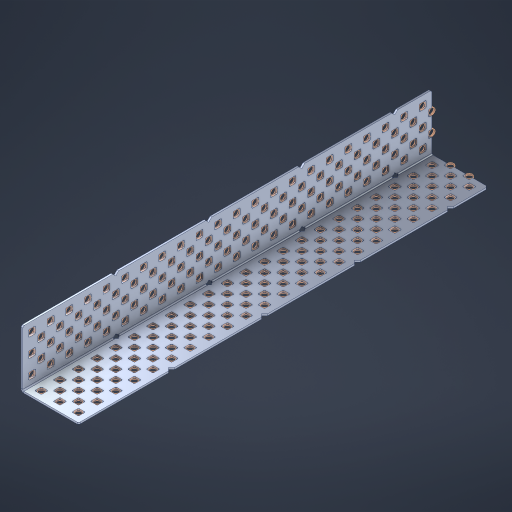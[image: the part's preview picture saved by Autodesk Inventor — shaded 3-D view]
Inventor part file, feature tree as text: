
AUTODESK INVENTOR PART (.ipt)
format: ipt  version: 2023 (Build 270158000, 158)  size: 2,348,544 bytes
history: native  units: in
note: dims shown in document units (in); Inventor stores cm internally (conversion verified against a paired STEP export)
features: other x226, extrude x218, sheet_metal_op x8, sketch x7, pattern_linear x3, mirror x1, chamfer x1
ambient origin geometry x8: Origin, YZ Plane, XZ Plane, XY Plane, X Axis, Y Axis, Z Axis, Center Point
bodies: Solid1 (feature_tree), Body (feature_tree)
feature tree (464):
  sheet_metal_op  "Flanges"
  sheet_metal_op  "Body Pattern"
  pattern_linear  "Center Double"  Spacing1=1.5in  [1 undecoded]
  pattern_linear  "Center Pattern"  Spacing1=0.1875in  [1 undecoded]
  other  "Arc Length"
  pattern_linear  "Notch Pattern"  Spacing1=0.0469in  [1 undecoded]
  other  "Diagonal Plane"
  mirror  "Everything Mirrored"
  chamfer  "End Chamfer"
  sketch  "Sketch1"  dims[d0=1.5in]
  other  "Plate1"
  sketch  "Sketch2"  dims[d1=11.0in]
  other  "Plate2"
  sheet_metal_op  "Bend1"
  sheet_metal_op  "Corner1"
  sketch  "Sketch8"  dims[d2=0.0469in]
  sketch  "Sketch9"  dims[d3=0.0469in]
  other  "Srf91"
  sheet_metal_op  "Body Pattern Sketch"
  other  "Srf92"
  sketch  "Sketch13"  dims[d4=0.0234in]
  sketch  "Sketch15"  dims[d5=0.0938in]
  sketch  "Sketch16"  dims[d6=0.0469in d7=1.5in d8=90.0deg d9=0.0312in d10=0.1875in d11=0.0469in d12=0.0469in d49=0.182in d50=0.02in d52=0.25in d53=0.0469in d54=0.0in d55=0.172in d56=1.0in d57=0.0in d85=0.1473in d86=0.1659in d89=0.0469in d90=0.0in d91=0.04in d92=0.0491in d95=2.5in d96=0.04in d97=0.25in d98=45.0deg d106=0.182in d107=0.02in d110=0.0469in d111=0.0in d112=0.172in d113=0.5in d114=0.0in d117=0.5in d126=0.0491in d127=0.1227in d128=0.08in d129=0.04in d130=2.5in d131=0.25in d132=8.6614in d134=0.5in d135=1.1811in d137=0.5in d140=0.5in d141=1.0in d142=0.3937in d144=0.5in d145=0.071in d146=0.7874in d148=0.5in]
  other  "Srf786"
  other  "Srf856"
  other  "Srf889"
  other  "Srf890"
  other  "Srf891"
  other  "Srf1275"
  other  "Srf1276"
  other  "Srf1278"
  other  "Srf1277"
  other  "Srf1285"
  other  "Srf1286"
  other  "Srf1287"
  other  "Srf1445"
  other  "Srf1446"
  other  "Srf1447"
  other  "Srf1448"
  other  "Srf1449"
  other  "Srf1537"
  other  "Srf1538"
  other  "Srf1539"
  other  "Srf1540"
  other  "Srf1541"
  other  "Srf1807"
  other  "Srf1808"
  other  "Srf1809"
  other  "Srf1810"
  other  "Srf1811"
  other  "Srf1812"
  other  "Srf1813"
  other  "Srf1814"
  other  "Srf1815"
  other  "Srf1816"
  other  "Srf1817"
  other  "Srf1818"
  other  "Srf1819"
  other  "Srf1959"
  other  "Srf1960"
  other  "Srf1961"
  other  "Srf1962"
  other  "Srf1963"
  other  "Srf1964"
  other  "Srf1965"
  other  "Srf1966"
  other  "Srf1967"
  other  "Srf1968"
  other  "Srf1969"
  other  "Srf1970"
  other  "Srf1971"
  other  "Srf2009"
  other  "Srf2010"
  other  "Srf2011"
  other  "Srf2012"
  other  "Srf2013"
  other  "Srf2014"
  other  "Srf2015"
  other  "Srf2016"
  other  "Srf2017"
  other  "Srf2018"
  other  "Srf2019"
  other  "Srf2020"
  other  "Srf2021"
  other  "Srf2022"
  other  "Srf2023"
  other  "Srf2024"
  other  "Srf2025"
  other  "Srf2026"
  other  "Srf2027"
  other  "Srf2028"
  other  "Srf2029"
  other  "Srf2030"
  other  "Srf2043"
  other  "Srf2044"
  other  "Srf2045"
  other  "Srf2046"
  other  "Srf2047"
  other  "Srf2048"
  other  "Srf2049"
  other  "Srf2050"
  other  "Srf2051"
  other  "Srf2052"
  other  "Srf2053"
  other  "Srf2054"
  other  "Srf2055"
  other  "Srf2056"
  other  "Srf2057"
  other  "Srf2058"
  other  "Srf2059"
  other  "Srf2060"
  other  "Srf2061"
  other  "Srf2062"
  other  "Srf2063"
  other  "Srf2076"
  other  "Srf2077"
  other  "Srf2078"
  other  "Srf2079"
  other  "Srf2080"
  other  "Srf2081"
  other  "Srf2082"
  other  "Srf2083"
  other  "Srf2084"
  other  "Srf2085"
  other  "Srf2086"
  other  "Srf2087"
  other  "Srf2088"
  other  "Srf2089"
  other  "Srf2090"
  other  "Srf2091"
  other  "Srf2092"
  other  "Srf2093"
  other  "Srf2094"
  other  "Srf2095"
  other  "Srf2096"
  other  "Srf2097"
  other  "Srf2098"
  other  "Srf2099"
  other  "Srf2100"
  other  "Srf2101"
  other  "Srf2102"
  other  "Srf2103"
  other  "Srf2104"
  other  "Srf2105"
  other  "Srf2106"
  other  "Srf2107"
  other  "Srf2108"
  other  "Srf2109"
  other  "Srf2110"
  other  "Srf2111"
  other  "Srf2112"
  other  "Srf2113"
  other  "Srf2114"
  other  "Srf2115"
  other  "Srf2116"
  other  "Srf2117"
  other  "Srf2118"
  other  "Srf2119"
  other  "Srf2120"
  other  "Srf2121"
  other  "Srf2122"
  other  "Srf2123"
  other  "Srf2124"
  other  "Srf2125"
  other  "Srf2126"
  other  "Srf2127"
  other  "Srf2128"
  other  "Srf2129"
  other  "Srf2130"
  other  "Srf2131"
  other  "Srf2132"
  other  "Srf2133"
  other  "Srf2134"
  other  "Srf2135"
  other  "Srf2136"
  other  "Srf2137"
  other  "Srf2138"
  other  "Srf2139"
  other  "Srf2179"
  other  "Srf2180"
  other  "Srf2181"
  other  "Srf2182"
  other  "Srf2183"
  other  "Srf2184"
  other  "Srf2185"
  other  "Srf2186"
  other  "Srf2187"
  other  "Srf2188"
  other  "Srf2189"
  other  "Srf2190"
  other  "Srf2191"
  other  "Srf2192"
  other  "Srf2193"
  other  "Srf2194"
  other  "Srf2195"
  other  "Srf2196"
  other  "Srf2197"
  other  "Srf2198"
  other  "Srf2199"
  other  "Srf2200"
  other  "Srf2201"
  other  "Srf2202"
  other  "Srf2203"
  other  "Srf2204"
  other  "Srf2205"
  other  "Srf2206"
  other  "Srf2207"
  other  "Srf2208"
  other  "Srf2209"
  other  "Srf2210"
  other  "Srf2211"
  other  "Srf2212"
  other  "Srf2213"
  other  "Srf2214"
  other  "Srf2215"
  other  "Srf2216"
  other  "Srf2217"
  other  "Srf2218"
  other  "Srf2219"
  other  "Srf2220"
  other  "Srf2221"
  other  "Srf2222"
  other  "Srf2223"
  other  "Srf2224"
  other  "Srf2225"
  other  "Srf2226"
  other  "Srf2227"
  other  "Srf2228"
  other  "Srf2229"
  other  "Srf2230"
  other  "Srf2231"
  other  "Srf2232"
  other  "Srf2233"
  other  "Srf2234"
  other  "Srf2235"
  other  "Srf2236"
  other  "Srf2237"
  other  "Srf2238"
  other  "Srf2239"
  other  "Srf2240"
  other  "Srf2241"
  sheet_metal_op  "Body Stamp"
  sheet_metal_op  "Body Circle"
  other  "Center Stamp"
  other  "Center Circle"
  sheet_metal_op  "Notch"
  extrude  "ExtrusionSrf92"  Depth=0.0469in
  extrude  "ExtrusionSrf856"  Depth=0.182in
  extrude  "ExtrusionSrf889"  Depth=0.02in
  extrude  "ExtrusionSrf890"  Depth=0.25in
  extrude  "ExtrusionSrf891"  Depth=0.0469in
  extrude  "ExtrusionSrf1275"  TaperAngle=0.0deg  [1 undecoded]
  extrude  "ExtrusionSrf1276"  Depth=0.5in
  extrude  "ExtrusionSrf1277"  Depth=1.0in TaperAngle=0.0deg
  extrude  "ExtrusionSrf1345"  Depth=0.5in
  extrude  "ExtrusionSrf1346"  Depth=0.5in
  extrude  "ExtrusionSrf1347"  Depth=0.0469in
  extrude  "ExtrusionSrf1348"  Depth=0.5in TaperAngle=0.0deg
  extrude  "ExtrusionSrf1445"  Depth=0.5in
  extrude  "ExtrusionSrf1446"  Depth=0.25in TaperAngle=45.0deg
  extrude  "ExtrusionSrf1447"  Depth=0.182in
  extrude  "ExtrusionSrf1448"  Depth=0.02in
  extrude  "ExtrusionSrf1449"  Depth=0.0469in
  extrude  "ExtrusionSrf1537"  TaperAngle=0.0deg  [1 undecoded]
  extrude  "ExtrusionSrf1538"  Depth=0.5in
  extrude  "ExtrusionSrf1539"  Depth=0.5in TaperAngle=0.0deg
  extrude  "ExtrusionSrf1540"  Depth=0.5in
  extrude  "ExtrusionSrf1541"  Depth=0.5in
  extrude  "ExtrusionSrf1807"  Depth=0.5in
  extrude  "ExtrusionSrf1808"  Depth=0.5in
  extrude  "ExtrusionSrf1809"  Depth=0.5in
  extrude  "ExtrusionSrf1810"  Depth=0.5in
  extrude  "ExtrusionSrf1811"  Depth=0.25in
  extrude  "ExtrusionSrf1812"  Depth=0.5in
  extrude  "ExtrusionSrf1813"  Depth=0.5in
  extrude  "ExtrusionSrf1814"  Depth=0.5in
  extrude  "ExtrusionSrf1815"  Depth=1.0in
  extrude  "ExtrusionSrf1816"  Depth=0.3937in
  extrude  "ExtrusionSrf1817"  Depth=0.5in
  extrude  "ExtrusionSrf1818"  Depth=0.5in
  extrude  "ExtrusionSrf1819"  [1 undecoded]
  extrude  "ExtrusionSrf1959"  [1 undecoded]
  extrude  "ExtrusionSrf1960"  [1 undecoded]
  extrude  "ExtrusionSrf1961"  [1 undecoded]
  extrude  "ExtrusionSrf1962"  [1 undecoded]
  extrude  "ExtrusionSrf1963"  [1 undecoded]
  extrude  "ExtrusionSrf1964"  [1 undecoded]
  extrude  "ExtrusionSrf1965"  [1 undecoded]
  extrude  "ExtrusionSrf1966"  [1 undecoded]
  extrude  "ExtrusionSrf1967"  [1 undecoded]
  extrude  "ExtrusionSrf1968"  [1 undecoded]
  extrude  "ExtrusionSrf1969"  [1 undecoded]
  extrude  "ExtrusionSrf1970"  [1 undecoded]
  extrude  "ExtrusionSrf1971"  [1 undecoded]
  extrude  "ExtrusionSrf2009"  [1 undecoded]
  extrude  "ExtrusionSrf2010"  [1 undecoded]
  extrude  "ExtrusionSrf2011"  [1 undecoded]
  extrude  "ExtrusionSrf2012"  [1 undecoded]
  extrude  "ExtrusionSrf2013"  [1 undecoded]
  extrude  "ExtrusionSrf2014"  [1 undecoded]
  extrude  "ExtrusionSrf2015"  [1 undecoded]
  extrude  "ExtrusionSrf2016"  [1 undecoded]
  extrude  "ExtrusionSrf2017"  [1 undecoded]
  extrude  "ExtrusionSrf2018"  [1 undecoded]
  extrude  "ExtrusionSrf2019"  [1 undecoded]
  extrude  "ExtrusionSrf2020"  [1 undecoded]
  extrude  "ExtrusionSrf2021"  [1 undecoded]
  extrude  "ExtrusionSrf2022"  [1 undecoded]
  extrude  "ExtrusionSrf2023"  [1 undecoded]
  extrude  "ExtrusionSrf2024"  [1 undecoded]
  extrude  "ExtrusionSrf2025"  [1 undecoded]
  extrude  "ExtrusionSrf2026"  [1 undecoded]
  extrude  "ExtrusionSrf2027"  [1 undecoded]
  extrude  "ExtrusionSrf2028"  [1 undecoded]
  extrude  "ExtrusionSrf2029"  [1 undecoded]
  extrude  "ExtrusionSrf2030"  [1 undecoded]
  extrude  "ExtrusionSrf2043"  [1 undecoded]
  extrude  "ExtrusionSrf2044"  [1 undecoded]
  extrude  "ExtrusionSrf2045"  [1 undecoded]
  extrude  "ExtrusionSrf2046"  [1 undecoded]
  extrude  "ExtrusionSrf2047"  [1 undecoded]
  extrude  "ExtrusionSrf2048"  [1 undecoded]
  extrude  "ExtrusionSrf2049"  [1 undecoded]
  extrude  "ExtrusionSrf2050"  [1 undecoded]
  extrude  "ExtrusionSrf2051"  [1 undecoded]
  extrude  "ExtrusionSrf2052"  [1 undecoded]
  extrude  "ExtrusionSrf2053"  [1 undecoded]
  extrude  "ExtrusionSrf2054"  [1 undecoded]
  extrude  "ExtrusionSrf2055"  [1 undecoded]
  extrude  "ExtrusionSrf2056"  [1 undecoded]
  extrude  "ExtrusionSrf2057"  [1 undecoded]
  extrude  "ExtrusionSrf2058"  [1 undecoded]
  extrude  "ExtrusionSrf2059"  [1 undecoded]
  extrude  "ExtrusionSrf2060"  [1 undecoded]
  extrude  "ExtrusionSrf2061"  [1 undecoded]
  extrude  "ExtrusionSrf2062"  [1 undecoded]
  extrude  "ExtrusionSrf2063"  [1 undecoded]
  extrude  "ExtrusionSrf2076"  [1 undecoded]
  extrude  "ExtrusionSrf2077"  [1 undecoded]
  extrude  "ExtrusionSrf2078"  [1 undecoded]
  extrude  "ExtrusionSrf2079"  [1 undecoded]
  extrude  "ExtrusionSrf2080"  [1 undecoded]
  extrude  "ExtrusionSrf2081"  [1 undecoded]
  extrude  "ExtrusionSrf2082"  [1 undecoded]
  extrude  "ExtrusionSrf2083"  [1 undecoded]
  extrude  "ExtrusionSrf2084"  [1 undecoded]
  extrude  "ExtrusionSrf2085"  [1 undecoded]
  extrude  "ExtrusionSrf2086"  [1 undecoded]
  extrude  "ExtrusionSrf2087"  [1 undecoded]
  extrude  "ExtrusionSrf2088"  [1 undecoded]
  extrude  "ExtrusionSrf2089"  [1 undecoded]
  extrude  "ExtrusionSrf2090"  [1 undecoded]
  extrude  "ExtrusionSrf2091"  [1 undecoded]
  extrude  "ExtrusionSrf2092"  [1 undecoded]
  extrude  "ExtrusionSrf2093"  [1 undecoded]
  extrude  "ExtrusionSrf2094"  [1 undecoded]
  extrude  "ExtrusionSrf2095"  [1 undecoded]
  extrude  "ExtrusionSrf2096"  [1 undecoded]
  extrude  "ExtrusionSrf2097"  [1 undecoded]
  extrude  "ExtrusionSrf2098"  [1 undecoded]
  extrude  "ExtrusionSrf2099"  [1 undecoded]
  extrude  "ExtrusionSrf2100"  [1 undecoded]
  extrude  "ExtrusionSrf2101"  [1 undecoded]
  extrude  "ExtrusionSrf2102"  [1 undecoded]
  extrude  "ExtrusionSrf2103"  [1 undecoded]
  extrude  "ExtrusionSrf2104"  [1 undecoded]
  extrude  "ExtrusionSrf2105"  [1 undecoded]
  extrude  "ExtrusionSrf2106"  [1 undecoded]
  extrude  "ExtrusionSrf2107"  [1 undecoded]
  extrude  "ExtrusionSrf2108"  [1 undecoded]
  extrude  "ExtrusionSrf2109"  [1 undecoded]
  extrude  "ExtrusionSrf2110"  [1 undecoded]
  extrude  "ExtrusionSrf2111"  [1 undecoded]
  extrude  "ExtrusionSrf2112"  [1 undecoded]
  extrude  "ExtrusionSrf2113"  [1 undecoded]
  extrude  "ExtrusionSrf2114"  [1 undecoded]
  extrude  "ExtrusionSrf2115"  [1 undecoded]
  extrude  "ExtrusionSrf2116"  [1 undecoded]
  extrude  "ExtrusionSrf2117"  [1 undecoded]
  extrude  "ExtrusionSrf2118"  [1 undecoded]
  extrude  "ExtrusionSrf2119"  [1 undecoded]
  extrude  "ExtrusionSrf2120"  [1 undecoded]
  extrude  "ExtrusionSrf2121"  [1 undecoded]
  extrude  "ExtrusionSrf2122"  [1 undecoded]
  extrude  "ExtrusionSrf2123"  [1 undecoded]
  extrude  "ExtrusionSrf2124"  [1 undecoded]
  extrude  "ExtrusionSrf2125"  [1 undecoded]
  extrude  "ExtrusionSrf2126"  [1 undecoded]
  extrude  "ExtrusionSrf2127"  [1 undecoded]
  extrude  "ExtrusionSrf2128"  [1 undecoded]
  extrude  "ExtrusionSrf2129"  [1 undecoded]
  extrude  "ExtrusionSrf2130"  [1 undecoded]
  extrude  "ExtrusionSrf2131"  [1 undecoded]
  extrude  "ExtrusionSrf2132"  [1 undecoded]
  extrude  "ExtrusionSrf2133"  [1 undecoded]
  extrude  "ExtrusionSrf2134"  [1 undecoded]
  extrude  "ExtrusionSrf2135"  [1 undecoded]
  extrude  "ExtrusionSrf2136"  [1 undecoded]
  extrude  "ExtrusionSrf2137"  [1 undecoded]
  extrude  "ExtrusionSrf2138"  [1 undecoded]
  extrude  "ExtrusionSrf2139"  [1 undecoded]
  extrude  "ExtrusionSrf2179"  [1 undecoded]
  extrude  "ExtrusionSrf2180"  [1 undecoded]
  extrude  "ExtrusionSrf2181"  [1 undecoded]
  extrude  "ExtrusionSrf2182"  [1 undecoded]
  extrude  "ExtrusionSrf2183"  [1 undecoded]
  extrude  "ExtrusionSrf2184"  [1 undecoded]
  extrude  "ExtrusionSrf2185"  [1 undecoded]
  extrude  "ExtrusionSrf2186"  [1 undecoded]
  extrude  "ExtrusionSrf2187"  [1 undecoded]
  extrude  "ExtrusionSrf2188"  [1 undecoded]
  extrude  "ExtrusionSrf2189"  [1 undecoded]
  extrude  "ExtrusionSrf2190"  [1 undecoded]
  extrude  "ExtrusionSrf2191"  [1 undecoded]
  extrude  "ExtrusionSrf2192"  [1 undecoded]
  extrude  "ExtrusionSrf2193"  [1 undecoded]
  extrude  "ExtrusionSrf2194"  [1 undecoded]
  extrude  "ExtrusionSrf2195"  [1 undecoded]
  extrude  "ExtrusionSrf2196"  [1 undecoded]
  extrude  "ExtrusionSrf2197"  [1 undecoded]
  extrude  "ExtrusionSrf2198"  [1 undecoded]
  extrude  "ExtrusionSrf2199"  [1 undecoded]
  extrude  "ExtrusionSrf2200"  [1 undecoded]
  extrude  "ExtrusionSrf2201"  [1 undecoded]
  extrude  "ExtrusionSrf2202"  [1 undecoded]
  extrude  "ExtrusionSrf2203"  [1 undecoded]
  extrude  "ExtrusionSrf2204"  [1 undecoded]
  extrude  "ExtrusionSrf2205"  [1 undecoded]
  extrude  "ExtrusionSrf2206"  [1 undecoded]
  extrude  "ExtrusionSrf2207"  [1 undecoded]
  extrude  "ExtrusionSrf2208"  [1 undecoded]
  extrude  "ExtrusionSrf2209"  [1 undecoded]
  extrude  "ExtrusionSrf2210"  [1 undecoded]
  extrude  "ExtrusionSrf2211"  [1 undecoded]
  extrude  "ExtrusionSrf2212"  [1 undecoded]
  extrude  "ExtrusionSrf2213"  [1 undecoded]
  extrude  "ExtrusionSrf2214"  [1 undecoded]
  extrude  "ExtrusionSrf2215"  [1 undecoded]
  extrude  "ExtrusionSrf2216"  [1 undecoded]
  extrude  "ExtrusionSrf2217"  [1 undecoded]
  extrude  "ExtrusionSrf2218"  [1 undecoded]
  extrude  "ExtrusionSrf2219"  [1 undecoded]
  extrude  "ExtrusionSrf2220"  [1 undecoded]
  extrude  "ExtrusionSrf2221"  [1 undecoded]
  extrude  "ExtrusionSrf2222"  [1 undecoded]
  extrude  "ExtrusionSrf2223"  [1 undecoded]
  extrude  "ExtrusionSrf2224"  [1 undecoded]
  extrude  "ExtrusionSrf2225"  [1 undecoded]
  extrude  "ExtrusionSrf2226"  [1 undecoded]
  extrude  "ExtrusionSrf2227"  [1 undecoded]
  extrude  "ExtrusionSrf2228"  [1 undecoded]
  extrude  "ExtrusionSrf2229"  [1 undecoded]
  extrude  "ExtrusionSrf2230"  [1 undecoded]
  extrude  "ExtrusionSrf2231"  [1 undecoded]
  extrude  "ExtrusionSrf2232"  [1 undecoded]
  extrude  "ExtrusionSrf2233"  [1 undecoded]
  extrude  "ExtrusionSrf2234"  [1 undecoded]
  extrude  "ExtrusionSrf2235"  [1 undecoded]
  extrude  "ExtrusionSrf2236"  [1 undecoded]
  extrude  "ExtrusionSrf2237"  [1 undecoded]
  extrude  "ExtrusionSrf2238"  [1 undecoded]
  extrude  "ExtrusionSrf2239"  [1 undecoded]
  extrude  "ExtrusionSrf2240"  [1 undecoded]
  extrude  "ExtrusionSrf2241"  [1 undecoded]
note: 189 required parameter values undecoded (feature->parameter linkage not recoverable at this tier; creation-order binding heuristic only, values carry confidence <= 0.55)
